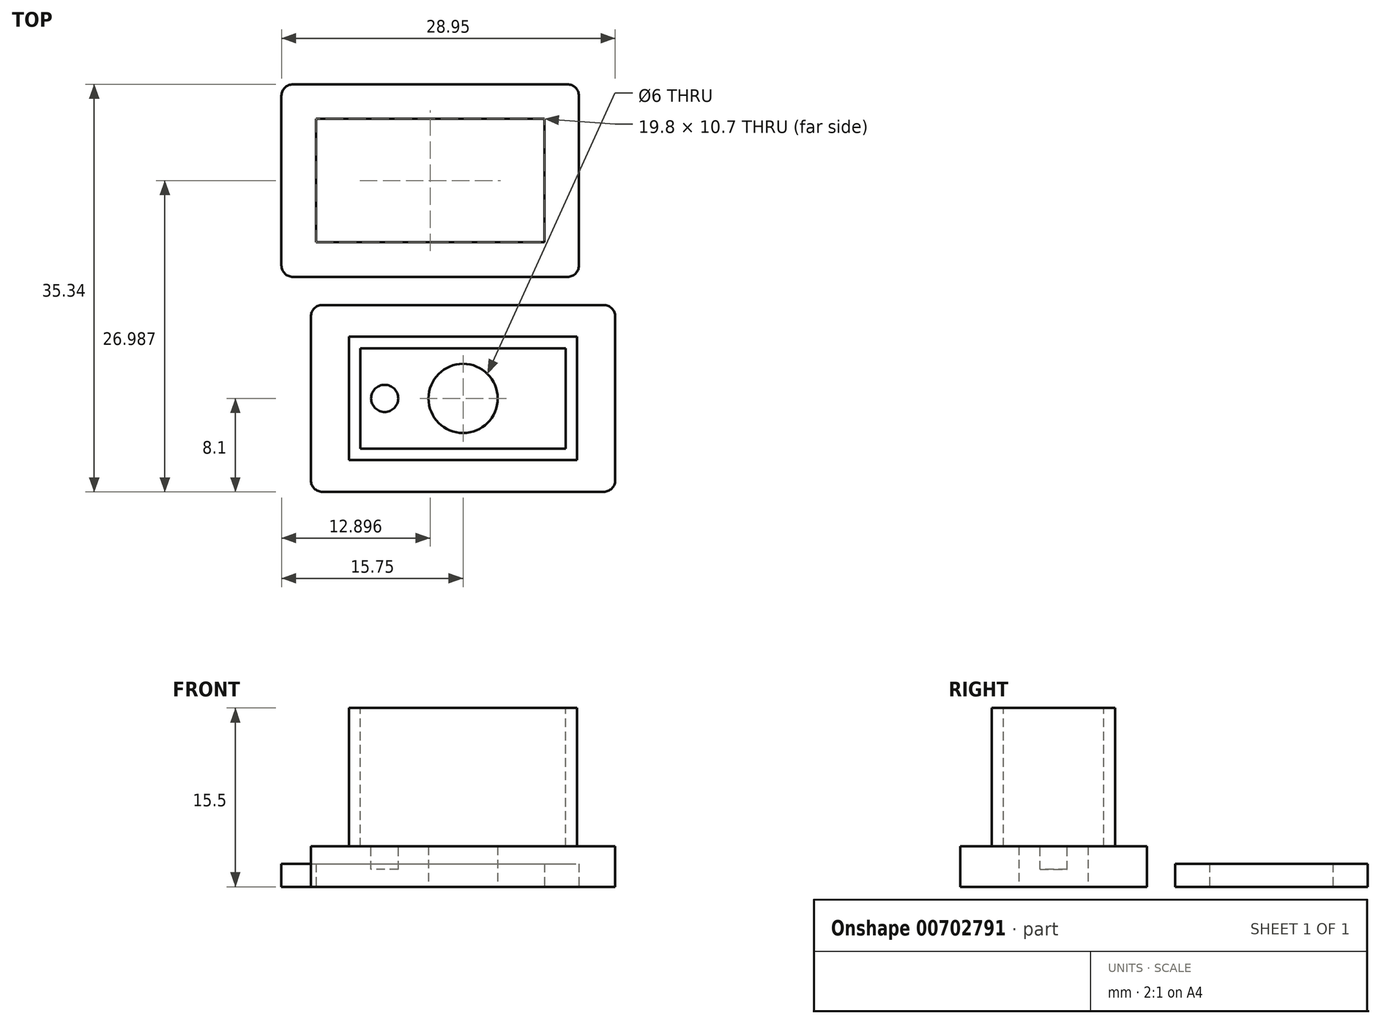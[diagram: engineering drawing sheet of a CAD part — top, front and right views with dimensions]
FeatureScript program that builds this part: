
annotation { "Feature Type Name" : "Feature", "Feature Type Description" : "" }
export const myFeature = defineFeature(function(context is Context, id is Id, definition is map)
    precondition{}
    {
        {
            var Q0;
            Q0=qCreatedBy(makeId("Top.planeOp"),FACE);
            var sketch = newSketch(context, id + "F0", { "sketchPlane" : qUnion([Q0])});
            skLineSegment(sketch, "E0.bottom", {"start": v(-13.2, 8.1) * mm, "end": v(13.2, 8.1) * mm});
            skLineSegment(sketch, "E0.top", {"start": v(-13.2, -8.1) * mm, "end": v(13.2, -8.1) * mm});
            skLineSegment(sketch, "E0.left", {"start": v(-13.2, 8.1) * mm, "end": v(-13.2, -8.1) * mm});
            skLineSegment(sketch, "E0.right", {"start": v(13.2, 8.1) * mm, "end": v(13.2, -8.1) * mm});
            skPoint(sketch, "E0.middle", {"position": v(0, 0) * mm});
            skSolve(sketch);
        }
        {
            var Q0;
            Q0 = qSketchRegion(id + "F0", true);
            extrude(context, id + "F1", {"entities" : qUnion([Q0]), "depth" : 3.5 * mm, "offsetDistance" : 25 * mm});
        }
        {
            var Q0;
            Q0=makeQuery(id+"F1.opExtrude","CAP_FACE",FACE,{"disambiguationData":[OSD([sQuery(id+"F0.wireOp",EDGE,"E0.bottom"),sQuery(id+"F0.wireOp",EDGE,"E0.top"),sQuery(id+"F0.wireOp",EDGE,"E0.left"),sQuery(id+"F0.wireOp",EDGE,"E0.right")])],"isStart":false});
            var sketch = newSketch(context, id + "F2", { "sketchPlane" : qUnion([Q0])});
            skLineSegment(sketch, "E1.bottom", {"start": v(-9.9, 5.35) * mm, "end": v(9.9, 5.35) * mm});
            skLineSegment(sketch, "E1.top", {"start": v(-9.9, -5.35) * mm, "end": v(9.9, -5.35) * mm});
            skLineSegment(sketch, "E1.left", {"start": v(-9.9, 5.35) * mm, "end": v(-9.9, -5.35) * mm});
            skLineSegment(sketch, "E1.right", {"start": v(9.9, 5.35) * mm, "end": v(9.9, -5.35) * mm});
            skPoint(sketch, "E1.middle", {"position": v(0, 0) * mm});
            skSolve(sketch);
        }
        {
            var Q0;
            Q0 = qSketchRegion(id + "F2", true);
            var Q1;
            Q1=makeQuery(id+"F2.imprint","IMPRINT",FACE,{"disambiguationData":[TD([[makeQuery(id+"F2.imprint","IMPRINT",EDGE,{"derivedFrom":sQuery(id+"F2.wireOp",EDGE,"E1.bottom")}),-1.0]])]});
            extrude(context, id + "F3", {"entities" : qUnion([Q0, Q1]), "operationType" : NewBodyOperationType.ADD, "depth" : 12 * mm, "offsetDistance" : 25 * mm});
        }
        {
            var Q0;
            Q0=makeQuery(id+"F3.opExtrude","CAP_FACE",FACE,{"disambiguationData":[OSD([sQuery(id+"F2.wireOp",EDGE,"E1.bottom"),sQuery(id+"F2.wireOp",EDGE,"E1.top"),sQuery(id+"F2.wireOp",EDGE,"E1.left"),sQuery(id+"F2.wireOp",EDGE,"E1.right")])],"isStart":false});
            var sketch = newSketch(context, id + "F4", { "sketchPlane" : qUnion([Q0])});
            skPoint(sketch, "E2", {"position": v(0, 0) * mm});
            skLineSegment(sketch, "E3.bottom", {"start": v(-8.9, 4.35) * mm, "end": v(8.9, 4.35) * mm});
            skLineSegment(sketch, "E3.top", {"start": v(-8.9, -4.35) * mm, "end": v(8.9, -4.35) * mm});
            skLineSegment(sketch, "E3.left", {"start": v(-8.9, 4.35) * mm, "end": v(-8.9, -4.35) * mm});
            skLineSegment(sketch, "E3.right", {"start": v(8.9, 4.35) * mm, "end": v(8.9, -4.35) * mm});
            skSolve(sketch);
        }
        {
            var Q0;
            Q0=makeQuery(id+"F4.imprint","IMPRINT",FACE,{"disambiguationData":[TD([[makeQuery(id+"F4.imprint","IMPRINT",EDGE,{"derivedFrom":sQuery(id+"F4.wireOp",EDGE,"E3.bottom")}),-1.0]])]});
            extrude(context, id + "F5", {"entities" : qUnion([Q0]), "operationType" : NewBodyOperationType.REMOVE, "oppositeDirection" : true, "depth" : 12 * mm, "offsetDistance" : 25 * mm});
        }
        {
            var Q0;
            Q0=makeQuery(id+"F1.opExtrude","CAP_FACE",FACE,{"disambiguationData":[OSD([sQuery(id+"F0.wireOp",EDGE,"E0.bottom"),sQuery(id+"F0.wireOp",EDGE,"E0.top"),sQuery(id+"F0.wireOp",EDGE,"E0.left"),sQuery(id+"F0.wireOp",EDGE,"E0.right")])],"isStart":true});
            var sketch = newSketch(context, id + "F6", { "sketchPlane" : qUnion([Q0])});
            skCircle(sketch, "E4", {"center": v(0, 0) * mm, "radius": 3 * mm});
            skSolve(sketch);
        }
        {
            var Q0;
            Q0 = qSketchRegion(id + "F6", true);
            extrude(context, id + "F7", {"entities" : qUnion([Q0]), "operationType" : NewBodyOperationType.REMOVE, "oppositeDirection" : true, "depth" : 25 * mm, "offsetDistance" : 25 * mm});
        }
        {
            var Q0;
            Q0=makeQuery(id+"F1.opExtrude","SWEPT_EDGE",EDGE,{"disambiguationData":[OSD([sQuery(id+"F0.wireOp",EDGE,"E0.bottom"),sQuery(id+"F0.wireOp",EDGE,"E0.right")])]});
            var Q1;
            Q1=makeQuery(id+"F1.opExtrude","SWEPT_EDGE",EDGE,{"disambiguationData":[OSD([sQuery(id+"F0.wireOp",EDGE,"E0.top"),sQuery(id+"F0.wireOp",EDGE,"E0.right")])]});
            var Q2;
            Q2=makeQuery(id+"F1.opExtrude","SWEPT_EDGE",EDGE,{"disambiguationData":[OSD([sQuery(id+"F0.wireOp",EDGE,"E0.bottom"),sQuery(id+"F0.wireOp",EDGE,"E0.left")])]});
            var Q3;
            Q3=makeQuery(id+"F1.opExtrude","SWEPT_EDGE",EDGE,{"disambiguationData":[OSD([sQuery(id+"F0.wireOp",EDGE,"E0.top"),sQuery(id+"F0.wireOp",EDGE,"E0.left")])]});
            fillet(context, id + "F8", {"entities" : qUnion([Q0, Q1, Q2, Q3]), "radius" : 1 * mm, "tangentPropagation" : true, "allowEdgeOverflow" : false});
        }
        {
            var Q0;
            Q0=makeQuery(id+"F5.boolean.opBoolean","COPY",FACE,{"derivedFrom":makeQuery(id+"F5.opExtrude","CAP_FACE",FACE,{"disambiguationData":[OSD([sQuery(id+"F4.wireOp",EDGE,"E3.bottom"),sQuery(id+"F4.wireOp",EDGE,"E3.top"),sQuery(id+"F4.wireOp",EDGE,"E3.left"),sQuery(id+"F4.wireOp",EDGE,"E3.right")])],"isStart":false})});
            var sketch = newSketch(context, id + "F9", { "sketchPlane" : qUnion([Q0])});
            skPoint(sketch, "E5", {"position": v(-6.8, 0) * mm});
            skCircle(sketch, "E6", {"center": v(-6.8, 0) * mm, "radius": 1.18 * mm});
            skSolve(sketch);
        }
        {
            var Q0;
            Q0=makeQuery(id+"F1.opExtrude","CAP_FACE",FACE,{"disambiguationData":[OSD([sQuery(id+"F0.wireOp",EDGE,"E0.bottom"),sQuery(id+"F0.wireOp",EDGE,"E0.top"),sQuery(id+"F0.wireOp",EDGE,"E0.left"),sQuery(id+"F0.wireOp",EDGE,"E0.right")])],"isStart":true});
            var Q1;
            Q1=makeQuery(id+"F9.imprint","IMPRINT",FACE,{"disambiguationData":[TD([[makeQuery(id+"F9.imprint","IMPRINT",EDGE,{"derivedFrom":sQuery(id+"F9.wireOp",EDGE,"E6")}),1.0]])]});
            extrude(context, id + "F10", {"entities" : qUnion([Q0, Q1]), "operationType" : NewBodyOperationType.REMOVE, "depth" : 2 * mm, "offsetDistance" : 25 * mm});
        }
        {
            var Q0;
            Q0=qCreatedBy(makeId("Top.planeOp"),FACE);
            var sketch = newSketch(context, id + "F11", { "sketchPlane" : qUnion([Q0])});
            skLineSegment(sketch, "E7.bottom", {"start": v(-12.75, 24.24) * mm, "end": v(7.05, 24.24) * mm});
            skLineSegment(sketch, "E7.top", {"start": v(-12.75, 13.54) * mm, "end": v(7.05, 13.54) * mm});
            skLineSegment(sketch, "E7.left", {"start": v(-12.75, 24.24) * mm, "end": v(-12.75, 13.54) * mm});
            skLineSegment(sketch, "E7.right", {"start": v(7.05, 24.24) * mm, "end": v(7.05, 13.54) * mm});
            skPoint(sketch, "E7.middle", {"position": v(-2.85, 18.89) * mm});
            skLineSegment(sketch, "E8.0", {"start": v(-14.75, 27.24) * mm, "end": v(9.05, 27.24) * mm});
            skLineSegment(sketch, "E8.1", {"start": v(-15.75, 26.24) * mm, "end": v(-15.75, 11.54) * mm});
            skLineSegment(sketch, "E8.2", {"start": v(-14.75, 10.54) * mm, "end": v(9.05, 10.54) * mm});
            skLineSegment(sketch, "E8.3", {"start": v(10.05, 26.24) * mm, "end": v(10.05, 11.54) * mm});
            skPoint(sketch, "E9.visualSharp", {"position": v(10.05, 27.24) * mm});
            skArc(sketch, "E9.filletArc", {"start": v(10.05, 26.24) * mm, "mid": v(9.75, 26.94) * mm, "end": v(9.05, 27.24) * mm});
            skPoint(sketch, "E10.visualSharp", {"position": v(-15.75, 27.24) * mm});
            skArc(sketch, "E10.filletArc", {"start": v(-14.75, 27.24) * mm, "mid": v(-15.46, 26.94) * mm, "end": v(-15.75, 26.24) * mm});
            skPoint(sketch, "E11.visualSharp", {"position": v(-15.75, 10.54) * mm});
            skArc(sketch, "E11.filletArc", {"start": v(-15.75, 11.54) * mm, "mid": v(-15.46, 10.83) * mm, "end": v(-14.75, 10.54) * mm});
            skPoint(sketch, "E12.visualSharp", {"position": v(10.05, 10.54) * mm});
            skArc(sketch, "E12.filletArc", {"start": v(9.05, 10.54) * mm, "mid": v(9.75, 10.83) * mm, "end": v(10.05, 11.54) * mm});
            skSolve(sketch);
        }
        {
            var Q0;
            Q0=makeQuery(id+"F11.imprint","IMPRINT",FACE,{"disambiguationData":[TD([[makeQuery(id+"F11.imprint","IMPRINT",EDGE,{"derivedFrom":sQuery(id+"F11.wireOp",EDGE,"E7.bottom")}),1.0]])]});
            extrude(context, id + "F12", {"entities" : qUnion([Q0]), "depth" : 2 * mm, "offsetDistance" : 25 * mm});
        }
    });
